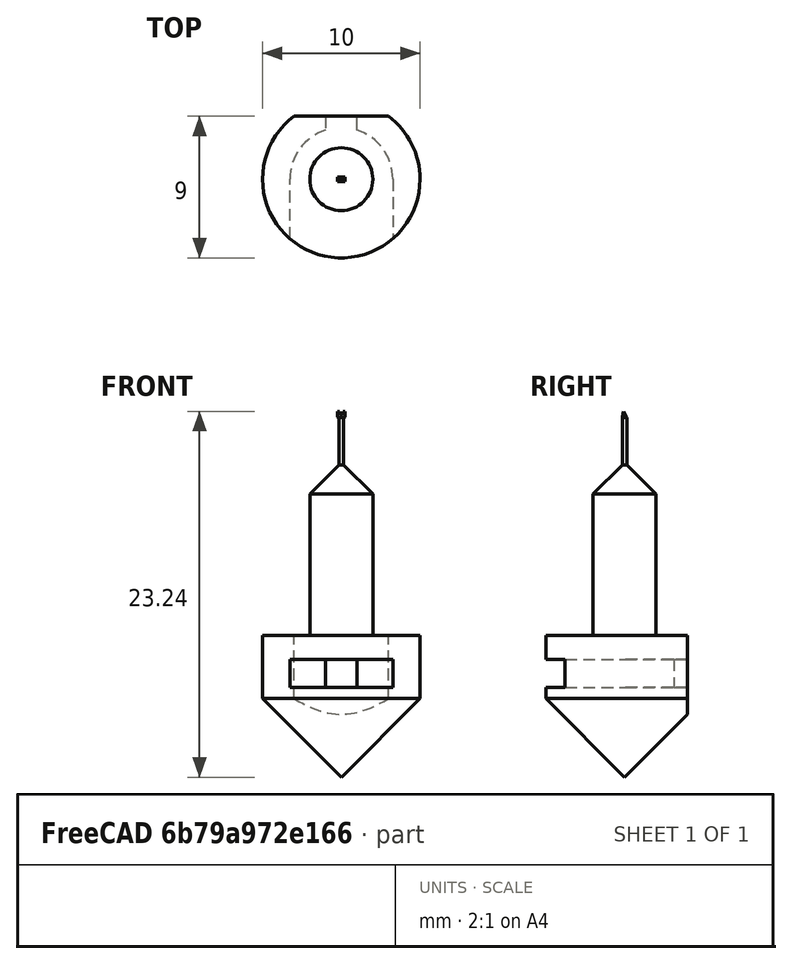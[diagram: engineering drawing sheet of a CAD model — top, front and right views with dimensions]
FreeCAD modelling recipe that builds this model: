
FCSTD DOCUMENT  (FreeCAD 0.18R16149 (Git))
Label: NeckWedge
License: All rights reserved
LicenseURL: http://en.wikipedia.org/wiki/All_rights_reserved
objects: Sketcher::SketchObject×6, PartDesign::Pocket×3, PartDesign::Revolution×2, PartDesign::Body×2, PartDesign::Chamfer×2, PartDesign::Pad×1, Mesh::Feature×1
note: 22 computed .brp shape members not serialized (recipe doc carries the construction recipe); baked Part::Feature solids carry a one-line shape summary decoded from their .brp

FEATURE [Sketcher::SketchObject] Sketch
  MapMode = 5
  Placement = pos=(0,0,0) rot=(1,0,0;1.5708rad)
  Support = -> [XZ_Plane]
  sketch-geometry (5):
    g0: LineSegment StartX=0 StartY=4.85 StartZ=0 EndX=0.15 EndY=4.85 EndZ=0
    g1: LineSegment StartX=0.15 StartY=4.85 StartZ=0 EndX=0.15 EndY=1.85 EndZ=0
    g2: LineSegment StartX=0 StartY=0 StartZ=0 EndX=0 EndY=4.85 EndZ=0
    g3: LineSegment StartX=0.15 StartY=1.85 StartZ=0 EndX=2 EndY=0 EndZ=0
    g4: LineSegment StartX=2 StartY=0 StartZ=0 EndX=0 EndY=0 EndZ=0
  constraints (14):
    c: Vertical(g1)
    c: Coincident(g2,g0)
    c: Horizontal(g0)
    c: Coincident(g0,g1)
    c: DistanceX(g0,g0) = 0.15
    c: DistanceY(g1,g1) = 3
    c: Vertical(g2)
    c: Coincident(g3,g1)
    c: PointOnObject(g3,g-1)
    c: Coincident(g4,g3)
    c: Coincident(g4,g-1)
    c: Coincident(g2,g4)
    c: DistanceX(g4,g4) = 2
    c: DistanceY(g-1,g0) = 4.85
FEATURE [PartDesign::Revolution] Revolution
  Angle = 360
  Axis = (-3e-16,3e-16,1)
  Base = (0,0,0)
  Placement = pos=(0,0,0) rot=(1,0,0;1.5708rad)
  Profile = -> Sketch
  ReferenceAxis = -> Z_Axis
  Reversed = true
FEATURE [Sketcher::SketchObject] Sketch007
  MapMode = 5
  Placement = pos=(0,0,0) rot=(1,0,0;1.5708rad)
  Support = -> [XZ_Plane004]
  sketch-geometry (6):
    g0: LineSegment StartX=0 StartY=0 StartZ=0 EndX=0 EndY=-18 EndZ=0
    g1: LineSegment StartX=0 StartY=-18 StartZ=0 EndX=5 EndY=-13 EndZ=0
    g2: LineSegment StartX=5 StartY=-13 StartZ=0 EndX=5 EndY=-9 EndZ=0
    g3: LineSegment StartX=5 StartY=-9 StartZ=0 EndX=2 EndY=-9 EndZ=0
    g4: LineSegment StartX=2 StartY=-9 StartZ=0 EndX=2 EndY=0 EndZ=0
    g5: LineSegment StartX=2 StartY=0 StartZ=0 EndX=0 EndY=0 EndZ=0
  constraints (17):
    c: Coincident(g0,g-1)
    c: Vertical(g0)
    c: Coincident(g1,g0)
    c: Coincident(g2,g1)
    c: Vertical(g2)
    c: Horizontal(g3)
    c: PointOnObject(g4,g-1)
    c: Vertical(g4)
    c: Coincident(g5,g4)
    c: Coincident(g5,g0)
    c: Coincident(g2,g3)
    c: Coincident(g3,g4)
    c: DistanceY(g4,g4) = 9
    c: DistanceX(g-1,g2) = 5
    c: DistanceY(g2,g2) = 4
    c: DistanceY(g0,g1) = 5
    c: DistanceX(g-1,g3) = 2
FEATURE [PartDesign::Revolution] Revolution001
  Angle = 360
  Axis = (0,2e-16,1)
  Base = (0,0,0)
  Placement = pos=(0,0,0) rot=(1,0,0;1.5708rad)
  Profile = -> Sketch007
  ReferenceAxis = -> Sketch007 [V_Axis]
  Reversed = true
FEATURE [Sketcher::SketchObject] Sketch008
  MapMode = 5
  Placement = pos=(0,-4e-15,-9) rot=(0,0,1;3.14159rad)
  Support = -> [Revolution001]
  sketch-geometry (4):
    g0: LineSegment StartX=-5 StartY=-4 StartZ=0 EndX=5 EndY=-4 EndZ=0
    g1: LineSegment StartX=5 StartY=-4 StartZ=0 EndX=5 EndY=-5.5 EndZ=0
    g2: LineSegment StartX=5 StartY=-5.5 StartZ=0 EndX=-5 EndY=-5.5 EndZ=0
    g3: LineSegment StartX=-5 StartY=-5.5 StartZ=0 EndX=-5 EndY=-4 EndZ=0
  constraints (12):
    c: Coincident(g0,g1)
    c: Coincident(g1,g2)
    c: Coincident(g2,g3)
    c: Coincident(g3,g0)
    c: Horizontal(g0)
    c: Horizontal(g2)
    c: Vertical(g1)
    c: Vertical(g3)
    c: DistanceY(g0,g-1) = 4
    c: Distance(g0) = 10
    c: Distance(g3) = 1.5
    c: DistanceX(g2,g-1) = 5
FEATURE [PartDesign::Pocket] Pocket004
  BaseFeature = -> Revolution001
  Length = 5
  Length2 = 100
  Placement = pos=(0,0,0) rot=(1,0,0;1.5708rad)
  Profile = -> Sketch008
  Type = 1
FEATURE [Sketcher::SketchObject] Sketch009
  AttachmentOffset = pos=(0,0,-1.5) rot=(0,0,1;0rad)
  MapMode = 5
  Placement = pos=(0,-4.6e-15,-10.5) rot=(0,0,1;3.14159rad)
  Support = -> [Pocket004]
  sketch-geometry (8):
    g0: ArcOfCircle CenterX=0 CenterY=0 CenterZ=0 NormalX=0 NormalY=0 NormalZ=1 AngleXU=0 Radius=3.275 StartAngle=3.14159 EndAngle=4.40209
    g1: LineSegment StartX=-3.275 StartY=4e-16 StartZ=0 EndX=-3.275 EndY=6.5 EndZ=0
    g2: LineSegment StartX=-3.275 StartY=6.5 StartZ=0 EndX=3.27 EndY=6.5 EndZ=0
    g3: LineSegment StartX=3.27 StartY=6.5 StartZ=0 EndX=3.27 EndY=-9e-16 EndZ=0
    g4: ArcOfCircle CenterX=0 CenterY=0 CenterZ=0 NormalX=0 NormalY=0 NormalZ=1 AngleXU=0 Radius=3.27 StartAngle=5.02318 EndAngle=6.28319
    g5: LineSegment StartX=-1 StartY=-3.11859 StartZ=0 EndX=-1 EndY=-6.5 EndZ=0
    g6: LineSegment StartX=-1 StartY=-6.5 StartZ=0 EndX=1 EndY=-6.5 EndZ=0
    g7: LineSegment StartX=1 StartY=-6.5 StartZ=0 EndX=1 EndY=-3.11334 EndZ=0
  constraints (22):
    c: Coincident(g0,g-1)
    c: Coincident(g2,g1)
    c: Horizontal(g2)
    c: Coincident(g3,g2)
    c: Radius(g0) = 3.275
    c: Tangent(g1,g0) = 1.5708
    c: Vertical(g1)
    c: DistanceY(g-1,g1) = 6.5
    c: Coincident(g4,g0)
    c: Vertical(g5)
    c: Coincident(g6,g5)
    c: Horizontal(g6)
    c: Coincident(g7,g6)
    c: Vertical(g7)
    c: Radius(g4) = 3.27
    c: Coincident(g4,g7)
    c: DistanceX(g5,g-1) = 1
    c: DistanceX(g-1,g6) = 1
    c: PointOnObject(g3,g-1)
    c: Tangent(g4,g3) = 1.5708
    c: Coincident(g0,g5)
    c: DistanceY(g5,g-1) = 6.5
FEATURE [PartDesign::Pocket] Pocket005
  BaseFeature = -> Pocket004
  Length = 1.8
  Length2 = 100
  Placement = pos=(0,0,0) rot=(1,0,0;1.5708rad)
  Profile = -> Sketch009
  Type = 0
FEATURE [PartDesign::Body] Body003  label="Magnet holder"
  Group = -> [Sketch007,Revolution001,Sketch008,Pocket004,Sketch009,Pocket005]
  Origin = -> Origin003
  Tip = -> Pocket005
FEATURE [Sketcher::SketchObject] Sketch010
  MapMode = 5
  Placement = pos=(0,0,0) rot=(0.57735,0.57735,0.57735;2.0944rad)
  Support = -> [YZ_Plane]
  sketch-geometry (3):
    g0: LineSegment StartX=0.15 StartY=4.85 StartZ=0 EndX=-0.15 EndY=4.85 EndZ=0
    g1: LineSegment StartX=-0.15 StartY=4.85 StartZ=0 EndX=-0.075 EndY=5.23971 EndZ=0
    g2: LineSegment StartX=-0.075 StartY=5.23971 StartZ=0 EndX=0.15 EndY=4.85 EndZ=0
  constraints (8):
    c: Coincident(g1,g0)
    c: Coincident(g2,g1)
    c: Coincident(g2,g0)
    c: Symmetric(g0,g0,g-2)
    c: DistanceX(g-1,g0) = 0.15
    c: Angle(g2,g0) = 1.0472
    c: DistanceY(g-1,g0) = 4.85
    c: DistanceX(g1,g-1) = 0.075
FEATURE [PartDesign::Pad] Pad
  BaseFeature = -> Revolution
  Length = 0.5
  Length2 = 100
  Midplane = true
  Placement = pos=(0,0,0) rot=(1,0,0;1.5708rad)
  Profile = -> Sketch010
  Type = 0
FEATURE [Sketcher::SketchObject] Sketch011
  MapMode = 5
  Placement = pos=(0,0,0) rot=(1,0,0;1.5708rad)
  Support = -> [XZ_Plane]
  sketch-geometry (4):
    g0: ArcOfCircle CenterX=0 CenterY=5.15 CenterZ=0 NormalX=0 NormalY=0 NormalZ=1 AngleXU=0 Radius=0.1 StartAngle=3.14159 EndAngle=6.28319
    g1: LineSegment StartX=-0.1 StartY=5.15 StartZ=0 EndX=-0.1 EndY=5.60565 EndZ=0
    g2: LineSegment StartX=-0.1 StartY=5.60565 StartZ=0 EndX=0.1 EndY=5.60565 EndZ=0
    g3: LineSegment StartX=0.1 StartY=5.60565 StartZ=0 EndX=0.1 EndY=5.15 EndZ=0
  constraints (10):
    c: PointOnObject(g0,g-2)
    c: Radius(g0) = 0.1
    c: Coincident(g2,g1)
    c: Horizontal(g2)
    c: Coincident(g3,g2)
    c: Tangent(g1,g0) = 1.5708
    c: Tangent(g3,g0) = 1.5708
    c: Vertical(g1)
    c: Vertical(g3)
    c: DistanceY(g-1,g0) = 5.15
FEATURE [PartDesign::Pocket] Pocket
  BaseFeature = -> Pad
  Length = 5
  Length2 = 100
  Midplane = true
  Placement = pos=(0,0,0) rot=(1,0,0;1.5708rad)
  Profile = -> Sketch011
  Type = 1
FEATURE [PartDesign::Chamfer] Chamfer
  Base = -> Pocket [Edge9]
  BaseFeature = -> Pocket
  Placement = pos=(0,0,0) rot=(1,0,0;1.5708rad)
  Size = 0.05
FEATURE [PartDesign::Chamfer] Chamfer001
  Base = -> Chamfer [Edge27]
  BaseFeature = -> Chamfer
  Placement = pos=(0,0,0) rot=(1,0,0;1.5708rad)
  Size = 0.05
FEATURE [PartDesign::Body] Body
  Group = -> [Sketch,Revolution,Sketch010,Pad,Sketch011,Pocket,Chamfer,Chamfer001]
  Origin = -> Origin
  Tip = -> Chamfer001
FEATURE [Mesh::Feature] Mesh003  label="Wedge"
